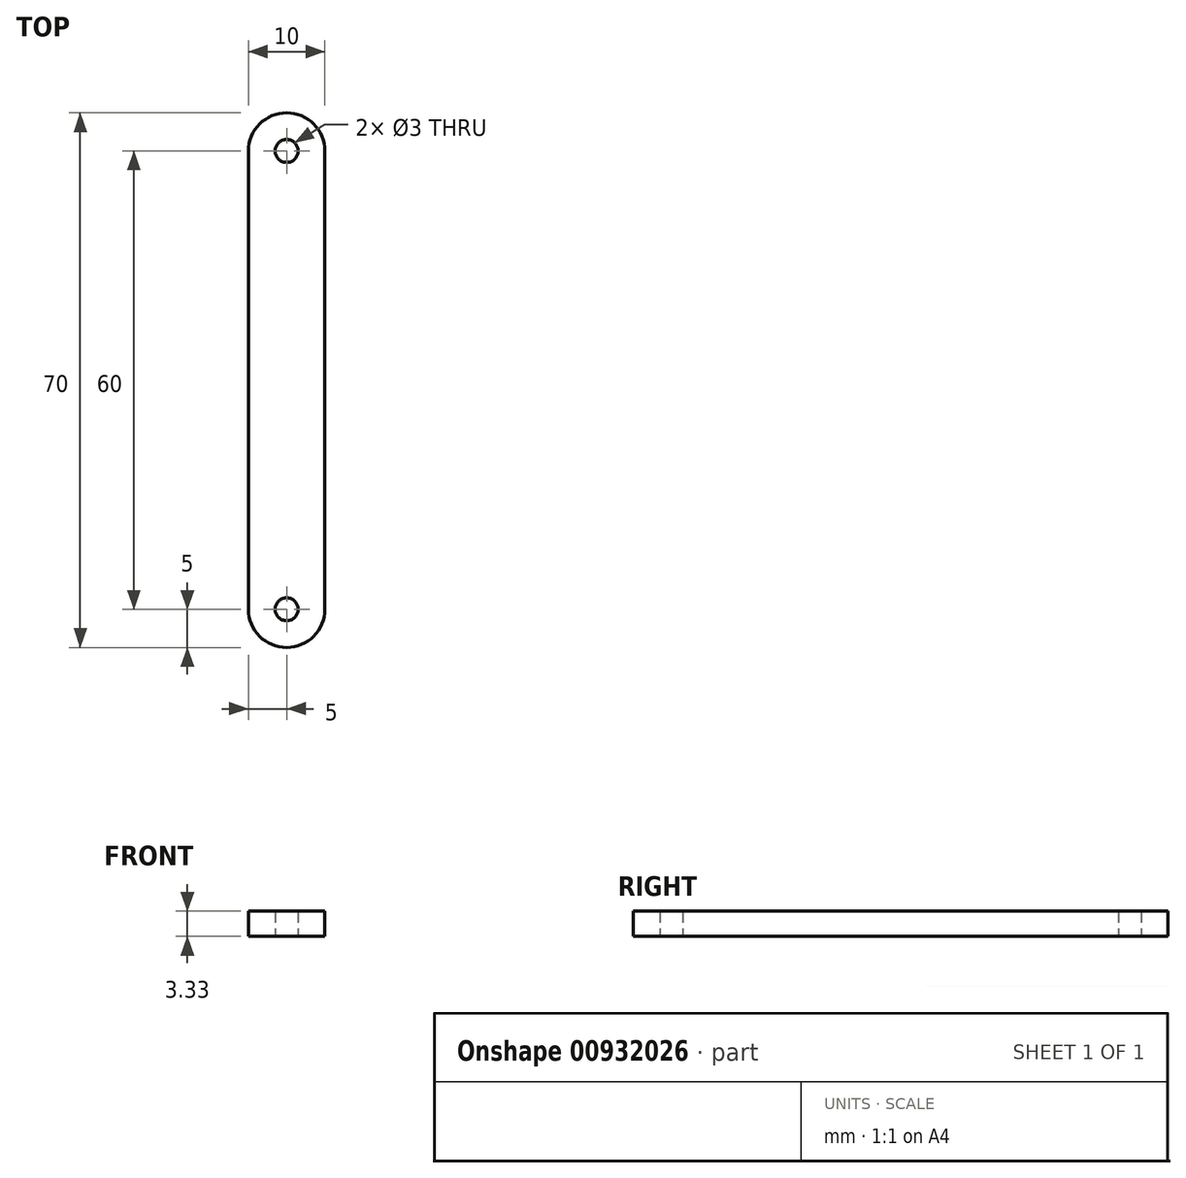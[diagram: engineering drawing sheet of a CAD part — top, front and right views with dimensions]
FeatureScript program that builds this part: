
annotation { "Feature Type Name" : "Feature", "Feature Type Description" : "" }
export const myFeature = defineFeature(function(context is Context, id is Id, definition is map)
    precondition{}
    {
        {
            var Q0;
            Q0=qCreatedBy(makeId("Top.planeOp"),FACE);
            var sketch = newSketch(context, id + "F0", { "sketchPlane" : qUnion([Q0])});
            skLineSegment(sketch, "E0.left", {"start": v(5, -30) * mm, "end": v(5, 30) * mm});
            skLineSegment(sketch, "E0.right", {"start": v(-5, -30) * mm, "end": v(-5, 30) * mm});
            skPoint(sketch, "E0.middle", {"position": v(0, 0) * mm});
            skArc(sketch, "E1", {"start": v(5, 30) * mm, "mid": v(0, 35) * mm, "end": v(-5, 30) * mm});
            skArc(sketch, "E2", {"start": v(-5, -30) * mm, "mid": v(0, -35) * mm, "end": v(5, -30) * mm});
            skCircle(sketch, "E3", {"center": v(0, 30) * mm, "radius": 1.5 * mm});
            skCircle(sketch, "E4", {"center": v(0, -30) * mm, "radius": 1.5 * mm});
            skSolve(sketch);
        }
        {
            var Q0;
            Q0=makeQuery(id+"F0.imprint","IMPRINT",FACE,{"disambiguationData":[TD([[makeQuery(id+"F0.imprint","IMPRINT",EDGE,{"derivedFrom":sQuery(id+"F0.wireOp",EDGE,"E0.left")}),1.0]])]});
            extrude(context, id + "F1", {"entities" : qUnion([Q0]), "depth" : 3.33 * mm, "offsetDistance" : 25 * mm});
        }
    });
